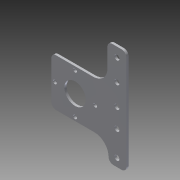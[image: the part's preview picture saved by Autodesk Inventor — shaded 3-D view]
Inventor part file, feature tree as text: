
AUTODESK INVENTOR PART (.ipt)
format: ipt  version: 2013 (Build 170138000, 138)  size: 150,016 bytes
history: native  units: in
note: dims shown in document units (in); Inventor stores cm internally (conversion verified against a paired STEP export)
features: chamfer x2, sketch x2, other x2, sheet_metal_op x1
ambient origin geometry x8: Origin, YZ Plane, XZ Plane, XY Plane, X Axis, Y Axis, Z Axis, Center Point
feature tree (7):
  sheet_metal_op  "Face2"
  chamfer  "Corner Round1"
  chamfer  "Corner Round2"
  sketch  "Sketch1"  dims[d0=2.5in]
  other  "Plate2"
  sketch  "Sketch4"  dims[d1=2.5in d6=0.2in d7=0.2in d8=0.2in d9=0.2in d10=0.12in d11=1.454in d12=1.125in d13=0.5in d15=1.0in d16=0.266in d17=0.266in d18=0.12in d19=0.12in d20=0.0in d23=2.0in d24=1.0in d25=2.25in d26=0.266in d27=0.266in d28=1.325in d29=0.266in d30=0.75in d31=0.25in]
  other  "Cut1"
